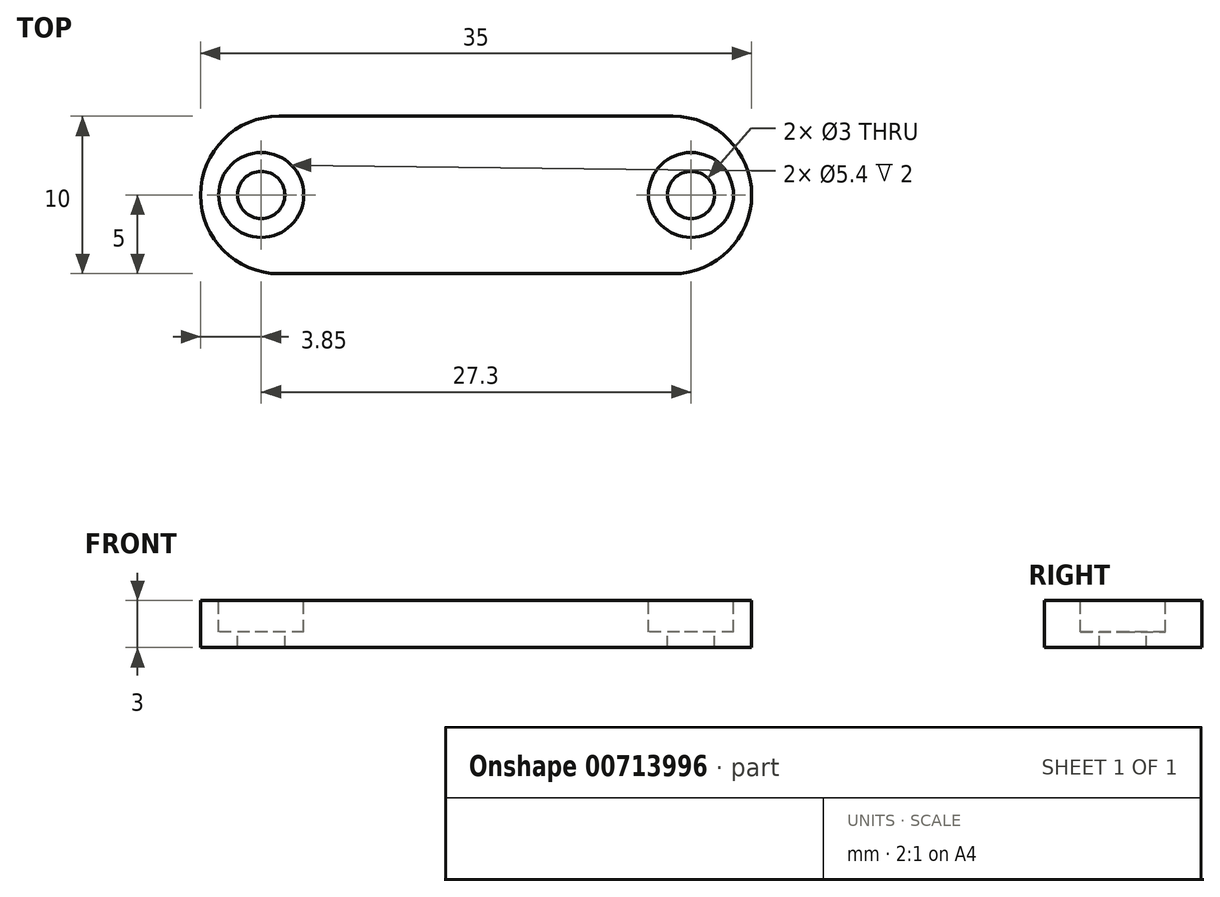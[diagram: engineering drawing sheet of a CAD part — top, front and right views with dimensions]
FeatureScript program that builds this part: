
annotation { "Feature Type Name" : "Feature", "Feature Type Description" : "" }
export const myFeature = defineFeature(function(context is Context, id is Id, definition is map)
    precondition{}
    {
        {
            var Q0;
            Q0=qCreatedBy(makeId("Top.planeOp"),FACE);
            var sketch = newSketch(context, id + "F0", { "sketchPlane" : qUnion([Q0])});
            skLineSegment(sketch, "E0.bottom", {"start": v(17.5, -5) * mm, "end": v(-17.5, -5) * mm});
            skLineSegment(sketch, "E0.top", {"start": v(17.5, 5) * mm, "end": v(-17.5, 5) * mm});
            skLineSegment(sketch, "E0.left", {"start": v(17.5, -5) * mm, "end": v(17.5, 5) * mm});
            skLineSegment(sketch, "E0.right", {"start": v(-17.5, -5) * mm, "end": v(-17.5, 5) * mm});
            skPoint(sketch, "E0.middle", {"position": v(0, 0) * mm});
            skLineSegment(sketch, "E1.bottom", {"start": v(13.65, -5) * mm, "end": v(-13.65, -5) * mm, "construction": true});
            skLineSegment(sketch, "E1.top", {"start": v(13.65, 5) * mm, "end": v(-13.65, 5) * mm, "construction": true});
            skLineSegment(sketch, "E1.left", {"start": v(13.65, -5) * mm, "end": v(13.65, 5) * mm, "construction": true});
            skLineSegment(sketch, "E1.right", {"start": v(-13.65, -5) * mm, "end": v(-13.65, 5) * mm, "construction": true});
            skPoint(sketch, "E2", {"position": v(-13.65, 0) * mm});
            skPoint(sketch, "E3", {"position": v(13.65, 0) * mm});
            skLineSegment(sketch, "E4.bottom", {"start": v(10, -2.5) * mm, "end": v(-10, -2.5) * mm});
            skLineSegment(sketch, "E4.top", {"start": v(10, 2.5) * mm, "end": v(-10, 2.5) * mm});
            skLineSegment(sketch, "E4.left", {"start": v(10, -2.5) * mm, "end": v(10, 2.5) * mm});
            skLineSegment(sketch, "E4.right", {"start": v(-10, -2.5) * mm, "end": v(-10, 2.5) * mm});
            skSolve(sketch);
        }
        {
            var Q0;
            Q0=makeQuery(id+"F0.imprint","IMPRINT",FACE,{"disambiguationData":[TD([[makeQuery(id+"F0.imprint","IMPRINT",EDGE,{"derivedFrom":sQuery(id+"F0.wireOp",EDGE,"E0.bottom")}),-1.0]])]});
            var Q1;
            Q1=makeQuery(id+"F0.imprint","IMPRINT",FACE,{"disambiguationData":[TD([[makeQuery(id+"F0.imprint","IMPRINT",EDGE,{"derivedFrom":sQuery(id+"F0.wireOp",EDGE,"E4.bottom")}),-1.0]])]});
            extrude(context, id + "F1", {"entities" : qUnion([Q0, Q1]), "depth" : 3 * mm, "offsetDistance" : 25 * mm});
        }
        {
            var Q0;
            Q0=qCreatedBy(makeId("Top.planeOp"),FACE);
            cPlane(context, id + "F2", {"entities" : qUnion([Q0]), "cplaneType" : CPlaneType.OFFSET, "offset" : 3 * mm, "width" : 150 * mm, "height" : 150 * mm});
        }
        {
            var Q0;
            Q0=qCreatedBy(id+"F2.planeOp",FACE);
            var sketch = newSketch(context, id + "F3", { "sketchPlane" : qUnion([Q0])});
            skPoint(sketch, "E5", {"position": v(-13.65, 0) * mm});
            skPoint(sketch, "E6", {"position": v(13.65, 0) * mm});
            skSolve(sketch);
        }
        {
            var Q0;
            Q0=sQuery(id+"F3.wireOp",VERTEX,"E5");
            var Q1;
            Q1=sQuery(id+"F3.wireOp",VERTEX,"E6");
            var Q2;
            Q2=makeQuery(id+"F1.opExtrude","SWEPT_BODY",BODY,{"disambiguationData":[OSD([sQuery(id+"F0.wireOp",EDGE,"E0.bottom"),sQuery(id+"F0.wireOp",EDGE,"E0.top"),sQuery(id+"F0.wireOp",EDGE,"E0.left"),sQuery(id+"F0.wireOp",EDGE,"E0.right"),sQuery(id+"F0.wireOp",EDGE,"E4.bottom"),sQuery(id+"F0.wireOp",EDGE,"E4.top"),sQuery(id+"F0.wireOp",EDGE,"E4.left"),sQuery(id+"F0.wireOp",EDGE,"E4.right")])]});
            hole(context, id + "F4", {"style" : HoleStyle.C_BORE, "endStyle" : HoleEndStyle.THROUGH, "holeDiameter" : 3 * mm, "cBoreDiameter" : 5.4 * mm, "cBoreDepth" : 2 * mm, "majorDiameter" : 5 * mm, "isTappedThrough" : true, "tappedDepth" : 12 * mm, "tapClearance" : 3, "startFromSketch" : true, "locations" : qUnion([Q0, Q1]), "scope" : qUnion([Q2])});
        }
        {
            var Q0;
            Q0=makeQuery(id+"F1.opExtrude","SWEPT_EDGE",EDGE,{"disambiguationData":[OSD([sQuery(id+"F0.wireOp",EDGE,"E0.bottom"),sQuery(id+"F0.wireOp",EDGE,"E0.right")])]});
            var Q1;
            Q1=makeQuery(id+"F1.opExtrude","SWEPT_EDGE",EDGE,{"disambiguationData":[OSD([sQuery(id+"F0.wireOp",EDGE,"E0.top"),sQuery(id+"F0.wireOp",EDGE,"E0.right")])]});
            var Q2;
            Q2=makeQuery(id+"F1.opExtrude","SWEPT_EDGE",EDGE,{"disambiguationData":[OSD([sQuery(id+"F0.wireOp",EDGE,"E0.top"),sQuery(id+"F0.wireOp",EDGE,"E0.left")])]});
            var Q3;
            Q3=makeQuery(id+"F1.opExtrude","SWEPT_EDGE",EDGE,{"disambiguationData":[OSD([sQuery(id+"F0.wireOp",EDGE,"E0.bottom"),sQuery(id+"F0.wireOp",EDGE,"E0.left")])]});
            fillet(context, id + "F5", {"entities" : qUnion([Q0, Q1, Q2, Q3]), "radius" : 5 * mm, "tangentPropagation" : true, "allowEdgeOverflow" : false});
        }
    });
